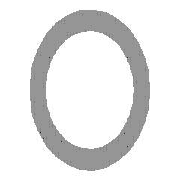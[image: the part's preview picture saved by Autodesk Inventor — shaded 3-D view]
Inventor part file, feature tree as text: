
AUTODESK INVENTOR PART (.ipt)
format: ipt  version: 2021 (Build 250183000, 183)  size: 260,608 bytes
history: native  units: mm (DEFAULTED — no unit token found)
features: other x11, plane x2, sketch x2, sweep x1
ambient origin geometry x8: Origin, YZ Plane, XZ Plane, XY Plane, X Axis, Y Axis, Z Axis, Center Point
bodies: Solid1 (feature_tree)
feature tree (16):
  parser-record x1  (decoder bookkeeping rows leaked as tree rows — omitted from the tree; the rows remain in map.json)
  other  "Driven Length"
  other  "Plano inicial"
  other  "Plano final"
  other  "Trayectoria de barrido"
  plane  "Plano de trabajo de orientación"
  sweep  "Cuerpo"
  sketch  "Sketch3"  dims[d0=26.67mm d1=2.8702mm]
  plane  "Work Plane3"
  sketch  "Sketch4"  dims[d4=-0.0mm d5=540.680242mm d6=90.0deg d7=540.680242mm d8=0.0mm d9=0.0mm d14=5.0mm d15=0.0mm d16=5.0mm d17=0.0mm]
  other  "Sup5"
  other  "Sup6"
  other  "Sólido3"
  other  "Sup4"
  other  "Superficie de contorno3"
  other  "Superficie de contorno4"
